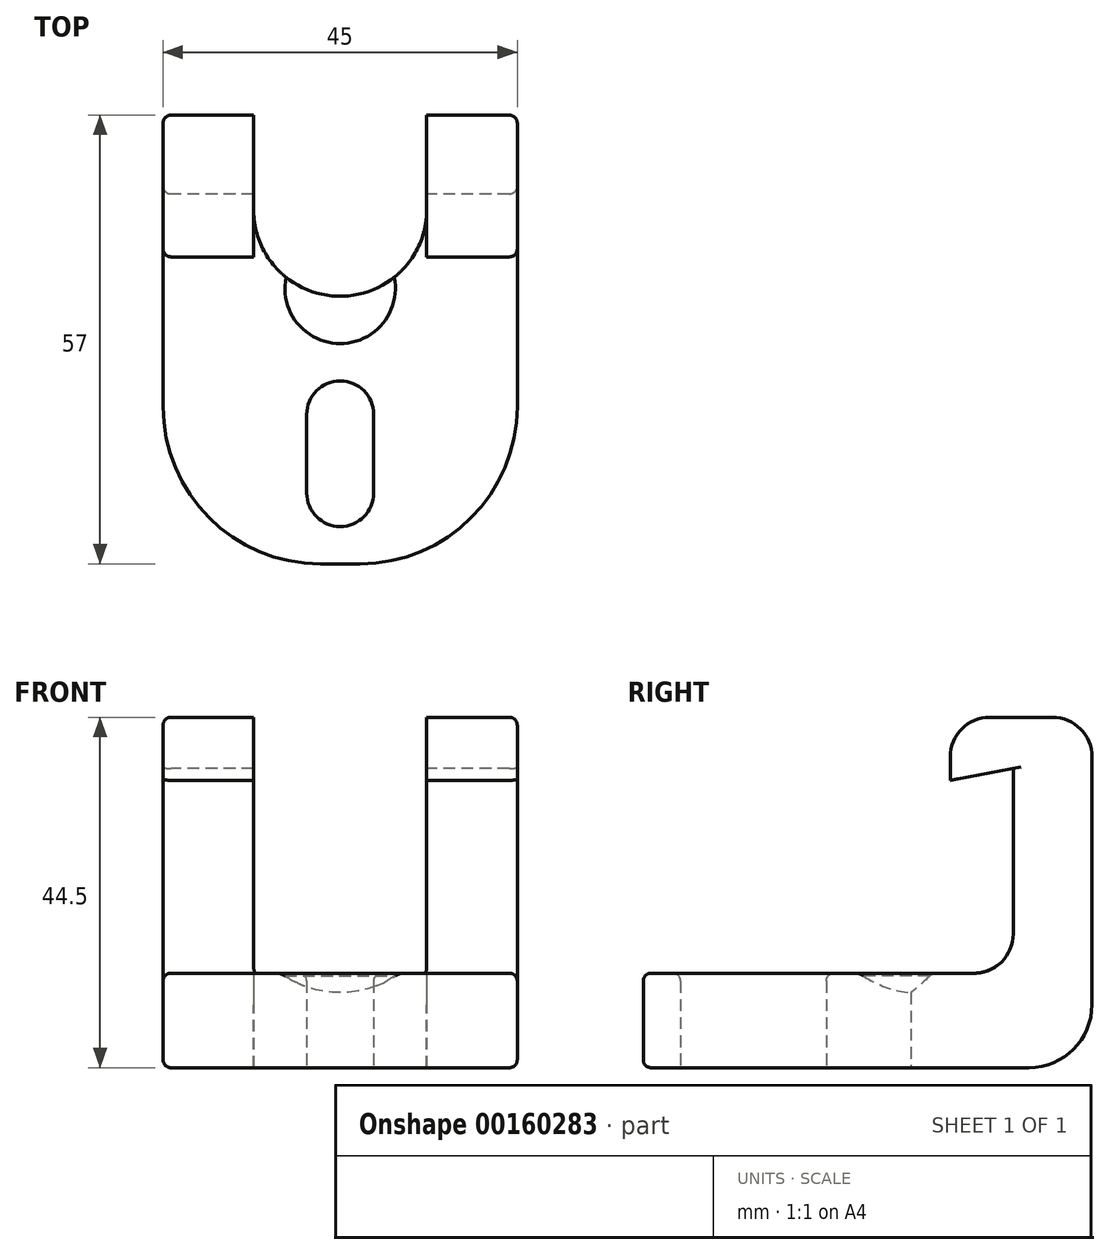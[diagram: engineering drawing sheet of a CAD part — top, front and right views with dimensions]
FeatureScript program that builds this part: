
annotation { "Feature Type Name" : "Feature", "Feature Type Description" : "" }
export const myFeature = defineFeature(function(context is Context, id is Id, definition is map)
    precondition{}
    {
        {
            var Q0;
            Q0=qCreatedBy(makeId("Right.planeOp"),FACE);
            var sketch = newSketch(context, id + "F0", { "sketchPlane" : qUnion([Q0])});
            skLineSegment(sketch, "E0", {"start": v(0, 0) * mm, "end": v(57, 0) * mm});
            skLineSegment(sketch, "E1", {"start": v(57, 0) * mm, "end": v(57, 44.5) * mm});
            skLineSegment(sketch, "E2", {"start": v(57, 44.5) * mm, "end": v(39, 44.5) * mm});
            skLineSegment(sketch, "E3", {"start": v(39, 44.5) * mm, "end": v(39, 36.5) * mm});
            skLineSegment(sketch, "E4", {"start": v(39, 36.5) * mm, "end": v(47, 38) * mm});
            skLineSegment(sketch, "E5", {"start": v(47, 38) * mm, "end": v(47, 12) * mm});
            skLineSegment(sketch, "E6", {"start": v(47, 12) * mm, "end": v(0, 12) * mm});
            skLineSegment(sketch, "E7", {"start": v(0, 12) * mm, "end": v(0, 0) * mm});
            skSolve(sketch);
        }
        {
            var Q0;
            Q0 = qSketchRegion(id + "F0", true);
            extrude(context, id + "F1", {"entities" : qUnion([Q0]), "depth" : 45 * mm});
        }
        {
            var Q0;
            Q0=makeQuery(id+"F1.opExtrude","SWEPT_FACE",FACE,{"disambiguationData":[OSD([sQuery(id+"F0.wireOp",EDGE,"E0")])]});
            var sketch = newSketch(context, id + "F2", { "sketchPlane" : qUnion([Q0])});
            skLineSegment(sketch, "E8.bottom", {"start": v(11.5, -57) * mm, "end": v(33.5, -57) * mm});
            skLineSegment(sketch, "E8.top", {"start": v(11.5, -45) * mm, "end": v(33.5, -45) * mm});
            skLineSegment(sketch, "E8.left", {"start": v(11.5, -57) * mm, "end": v(11.5, -45) * mm});
            skLineSegment(sketch, "E8.right", {"start": v(33.5, -57) * mm, "end": v(33.5, -45) * mm});
            skArc(sketch, "E9", {"start": v(33.5, -45) * mm, "mid": v(22.5, -34) * mm, "end": v(11.5, -45) * mm});
            skSolve(sketch);
        }
        {
            var Q0;
            Q0 = qSketchRegion(id + "F2", true);
            var Q1;
            Q1=makeQuery(id+"F1.opExtrude","SWEPT_FACE",FACE,{"disambiguationData":[OSD([sQuery(id+"F0.wireOp",EDGE,"E4")])]});
            extrude(context, id + "F3", {"entities" : qUnion([Q0]), "operationType" : NewBodyOperationType.REMOVE, "endBound" : BoundingType.UP_TO_SURFACE, "oppositeDirection" : true, "endBoundEntityFace" : qUnion([Q1]), "depth" : 25 * mm});
        }
        {
            var Q0;
            Q0=makeQuery(id+"F1.opExtrude","SWEPT_FACE",FACE,{"disambiguationData":[OSD([sQuery(id+"F0.wireOp",EDGE,"E1")])]});
            var sketch = newSketch(context, id + "F4", { "sketchPlane" : qUnion([Q0])});
            skLineSegment(sketch, "E10.bottom", {"start": v(-33.5, 31) * mm, "end": v(-11.5, 31) * mm});
            skLineSegment(sketch, "E10.top", {"start": v(-33.5, 44.5) * mm, "end": v(-11.5, 44.5) * mm});
            skLineSegment(sketch, "E10.left", {"start": v(-33.5, 31) * mm, "end": v(-33.5, 44.5) * mm});
            skLineSegment(sketch, "E10.right", {"start": v(-11.5, 31) * mm, "end": v(-11.5, 44.5) * mm});
            skSolve(sketch);
        }
        {
            var Q0;
            Q0 = qSketchRegion(id + "F4", true);
            extrude(context, id + "F5", {"entities" : qUnion([Q0]), "operationType" : NewBodyOperationType.REMOVE, "oppositeDirection" : true, "depth" : 25 * mm});
        }
        {
            var Q0;
            Q0=makeQuery(id+"F1.opExtrude","SWEPT_FACE",FACE,{"disambiguationData":[OSD([sQuery(id+"F0.wireOp",EDGE,"E0")])]});
            var sketch = newSketch(context, id + "F6", { "sketchPlane" : qUnion([Q0])});
            skCircle(sketch, "E11", {"center": v(22.5, -9) * mm, "radius": 4.25 * mm});
            skPoint(sketch, "E11.centerSnap0", {"position": v(22.5, 0) * mm});
            skLineSegment(sketch, "E12.bottom", {"start": v(18.25, -9) * mm, "end": v(26.75, -9) * mm});
            skLineSegment(sketch, "E12.top", {"start": v(18.25, -19) * mm, "end": v(26.75, -19) * mm});
            skLineSegment(sketch, "E12.left", {"start": v(18.25, -9) * mm, "end": v(18.25, -19) * mm});
            skLineSegment(sketch, "E12.right", {"start": v(26.75, -9) * mm, "end": v(26.75, -19) * mm});
            skCircle(sketch, "E13", {"center": v(22.5, -19) * mm, "radius": 4.25 * mm});
            skSolve(sketch);
        }
        {
            var Q0;
            {var subQ0=sQuery(id+"F6.wireOp",EDGE,"E12.bottom");Q0=makeQuery(id+"F6.imprint","IMPRINT",FACE,{"disambiguationData":[TD([[makeQuery(id+"F6.imprint","IMPRINT",EDGE,{"derivedFrom":subQ0}),1.0]])]});}
            var Q1;
            {var subQ0=sQuery(id+"F6.wireOp",EDGE,"E12.bottom");Q1=makeQuery(id+"F6.imprint","IMPRINT",FACE,{"disambiguationData":[TD([[makeQuery(id+"F6.imprint","IMPRINT",EDGE,{"derivedFrom":subQ0}),-1.0]])]});}
            var Q2;
            {var subQ0=sQuery(id+"F6.wireOp",EDGE,"E13");var subQ1=sQuery(id+"F6.wireOp",EDGE,"E11");var subQ2=makeQuery(id+"F6.imprint","INTERSECT",VERTEX,{"disambiguationData":[OD(0.0)],"derivedFrom":[subQ1,subQ0]});Q2=makeQuery(id+"F6.imprint","IMPRINT",FACE,{"disambiguationData":[TD([[makeQuery(id+"F6.imprint","IMPRINT",EDGE,{"disambiguationData":[TD([[subQ2,-1.0]])],"derivedFrom":subQ1}),1.0]])]});}
            var Q3;
            {var subQ0=sQuery(id+"F6.wireOp",EDGE,"E12.left");Q3=makeQuery(id+"F6.imprint","IMPRINT",FACE,{"disambiguationData":[TD([[makeQuery(id+"F6.imprint","IMPRINT",EDGE,{"derivedFrom":subQ0}),1.0]])]});}
            var Q4;
            {var subQ4=sQuery(id+"F6.wireOp",EDGE,"E12.top");Q4=makeQuery(id+"F6.imprint","IMPRINT",FACE,{"disambiguationData":[TD([[makeQuery(id+"F6.imprint","IMPRINT",EDGE,{"derivedFrom":subQ4}),1.0]])]});}
            var Q5;
            {var subQ0=sQuery(id+"F6.wireOp",EDGE,"E12.right");Q5=makeQuery(id+"F6.imprint","IMPRINT",FACE,{"disambiguationData":[TD([[makeQuery(id+"F6.imprint","IMPRINT",EDGE,{"derivedFrom":subQ0}),-1.0]])]});}
            var Q6;
            {var subQ0=sQuery(id+"F6.wireOp",EDGE,"E12.top");Q6=makeQuery(id+"F6.imprint","IMPRINT",FACE,{"disambiguationData":[TD([[makeQuery(id+"F6.imprint","IMPRINT",EDGE,{"derivedFrom":subQ0}),-1.0]])]});}
            extrude(context, id + "F7", {"entities" : qUnion([Q0, Q1, Q2, Q3, Q4, Q5, Q6]), "operationType" : NewBodyOperationType.REMOVE, "oppositeDirection" : true, "depth" : 25 * mm});
        }
        {
            var Q0;
            Q0=makeQuery(id+"F3.boolean.opBoolean","INTERSECT",EDGE,{"derivedFrom":[makeQuery(id+"F1.opExtrude","SWEPT_FACE",FACE,{"disambiguationData":[OSD([sQuery(id+"F0.wireOp",EDGE,"E6")])]}),makeQuery(id+"F3.opExtrude","SWEPT_FACE",FACE,{"disambiguationData":[OSD([sQuery(id+"F2.wireOp",EDGE,"E9")])]})]});
            cPoint(context, id + "F8", {"entities" : qUnion([Q0]), "parameter" : 0.5});
        }
        {
            var Q0;
            Q0=qCreatedBy(makeId("Right.planeOp"),FACE);
            var Q1;
            Q1 = qCreatedBy(id + "F8" ,VERTEX);
            cPlane(context, id + "F9", {"entities" : qUnion([Q0, Q1]), "cplaneType" : CPlaneType.PLANE_POINT, "offset" : 25 * mm, "width" : 150 * mm, "height" : 150 * mm});
        }
        {
            var Q0;
            Q0=qCreatedBy(id+"F9.planeOp",FACE);
            var sketch = newSketch(context, id + "F10", { "sketchPlane" : qUnion([Q0])});
            skCircle(sketch, "E14", {"center": v(35, 22) * mm, "radius": 12.5 * mm});
            skLineSegment(sketch, "E15", {"start": v(22.5, 22) * mm, "end": v(47.5, 22) * mm});
            skSolve(sketch);
        }
        {
            var Q0;
            {var subQ0=sQuery(id+"F10.wireOp",EDGE,"E15");Q0=makeQuery(id+"F10.imprint","IMPRINT",FACE,{"disambiguationData":[TD([[makeQuery(id+"F10.imprint","IMPRINT",EDGE,{"derivedFrom":subQ0}),-1.0]])]});}
            var Q1;
            Q1=sQuery(id+"F10.wireOp",EDGE,"E15");
            revolve(context, id + "F11", {"operationType" : NewBodyOperationType.REMOVE, "entities" : qUnion([Q0]), "axis" : qUnion([Q1]), "revolveType" : RevolveType.FULL, "oppositeDirection" : true});
        }
        {
            var Q0;
            Q0=makeQuery(id+"F1.opExtrude","CAP_EDGE",EDGE,{"disambiguationData":[OSD([sQuery(id+"F0.wireOp",EDGE,"E7")])],"isStart":false});
            var Q1;
            Q1=makeQuery(id+"F1.opExtrude","CAP_EDGE",EDGE,{"disambiguationData":[OSD([sQuery(id+"F0.wireOp",EDGE,"E7")])],"isStart":true});
            fillet(context, id + "F12", {"entities" : qUnion([Q0, Q1]), "radius" : 20 * mm, "tangentPropagation" : true, "allowEdgeOverflow" : false});
        }
        {
            var Q0;
            Q0=makeQuery(id+"F11.boolean.opBoolean","INTERSECT",EDGE,{"derivedFrom":[makeQuery(id+"F1.opExtrude","SWEPT_FACE",FACE,{"disambiguationData":[OSD([sQuery(id+"F0.wireOp",EDGE,"E6")])]}),makeQuery(id+"F11.opRevolve","SWEPT_FACE",FACE,{"disambiguationData":[OSD([sQuery(id+"F10.wireOp",EDGE,"E14")])]})]});
            fillet(context, id + "F13", {"entities" : qUnion([Q0]), "radius" : 2 * mm, "tangentPropagation" : true, "allowEdgeOverflow" : false});
        }
        {
            var Q0;
            {var subQ0=sQuery(id+"F0.wireOp",EDGE,"E6");var subQ1=sQuery(id+"F0.wireOp",EDGE,"E5");Q0=makeQuery(id+"F3.boolean.opBoolean","SPLIT",EDGE,{"disambiguationData":[TD([makeQuery(id+"F3.opExtrude","SWEPT_FACE",FACE,{"disambiguationData":[OSD([sQuery(id+"F2.wireOp",EDGE,"E8.left")])]})])],"derivedFrom":makeQuery(id+"F1.opExtrude","SWEPT_EDGE",EDGE,{"disambiguationData":[OSD([subQ1,subQ0])]})});}
            var Q1;
            {var subQ0=sQuery(id+"F0.wireOp",EDGE,"E6");var subQ1=sQuery(id+"F0.wireOp",EDGE,"E5");Q1=makeQuery(id+"F3.boolean.opBoolean","SPLIT",EDGE,{"disambiguationData":[TD([makeQuery(id+"F3.opExtrude","SWEPT_FACE",FACE,{"disambiguationData":[OSD([sQuery(id+"F2.wireOp",EDGE,"E8.right")])]})])],"derivedFrom":makeQuery(id+"F1.opExtrude","SWEPT_EDGE",EDGE,{"disambiguationData":[OSD([subQ1,subQ0])]})});}
            var Q2;
            {var subQ0=sQuery(id+"F0.wireOp",EDGE,"E2");var subQ1=sQuery(id+"F0.wireOp",EDGE,"E1");Q2=makeQuery(id+"F5.boolean.opBoolean","SPLIT",EDGE,{"disambiguationData":[TD([makeQuery(id+"F3.boolean.opBoolean","COPY",FACE,{"derivedFrom":makeQuery(id+"F3.opExtrude","SWEPT_FACE",FACE,{"disambiguationData":[OSD([sQuery(id+"F2.wireOp",EDGE,"E8.left")])]})})])],"derivedFrom":makeQuery(id+"F1.opExtrude","SWEPT_EDGE",EDGE,{"disambiguationData":[OSD([subQ1,subQ0])]})});}
            var Q3;
            {var subQ0=sQuery(id+"F0.wireOp",EDGE,"E2");var subQ1=sQuery(id+"F0.wireOp",EDGE,"E1");Q3=makeQuery(id+"F5.boolean.opBoolean","SPLIT",EDGE,{"disambiguationData":[TD([makeQuery(id+"F3.boolean.opBoolean","COPY",FACE,{"derivedFrom":makeQuery(id+"F3.opExtrude","SWEPT_FACE",FACE,{"disambiguationData":[OSD([sQuery(id+"F2.wireOp",EDGE,"E8.right")])]})})])],"derivedFrom":makeQuery(id+"F1.opExtrude","SWEPT_EDGE",EDGE,{"disambiguationData":[OSD([subQ1,subQ0])]})});}
            var Q4;
            {var subQ0=sQuery(id+"F0.wireOp",EDGE,"E3");var subQ1=sQuery(id+"F0.wireOp",EDGE,"E2");Q4=makeQuery(id+"F5.boolean.opBoolean","SPLIT",EDGE,{"disambiguationData":[TD([makeQuery(id+"F3.boolean.opBoolean","COPY",FACE,{"derivedFrom":makeQuery(id+"F3.opExtrude","SWEPT_FACE",FACE,{"disambiguationData":[OSD([sQuery(id+"F2.wireOp",EDGE,"E8.left")])]})})])],"derivedFrom":makeQuery(id+"F1.opExtrude","SWEPT_EDGE",EDGE,{"disambiguationData":[OSD([subQ1,subQ0])]})});}
            var Q5;
            {var subQ0=sQuery(id+"F0.wireOp",EDGE,"E3");var subQ1=sQuery(id+"F0.wireOp",EDGE,"E2");Q5=makeQuery(id+"F5.boolean.opBoolean","SPLIT",EDGE,{"disambiguationData":[TD([makeQuery(id+"F3.boolean.opBoolean","COPY",FACE,{"derivedFrom":makeQuery(id+"F3.opExtrude","SWEPT_FACE",FACE,{"disambiguationData":[OSD([sQuery(id+"F2.wireOp",EDGE,"E8.right")])]})})])],"derivedFrom":makeQuery(id+"F1.opExtrude","SWEPT_EDGE",EDGE,{"disambiguationData":[OSD([subQ1,subQ0])]})});}
            fillet(context, id + "F14", {"entities" : qUnion([Q0, Q1, Q2, Q3, Q4, Q5]), "radius" : 5 * mm, "tangentPropagation" : true, "allowEdgeOverflow" : false});
        }
        {
            var Q0;
            {var subQ0=sQuery(id+"F0.wireOp",EDGE,"E0");var subQ1=sQuery(id+"F0.wireOp",EDGE,"E1");Q0=makeQuery(id+"F3.boolean.opBoolean","SPLIT",EDGE,{"disambiguationData":[TD([makeQuery(id+"F3.opExtrude","SWEPT_FACE",FACE,{"disambiguationData":[OSD([sQuery(id+"F2.wireOp",EDGE,"E8.right")])]})])],"derivedFrom":makeQuery(id+"F1.opExtrude","SWEPT_EDGE",EDGE,{"disambiguationData":[OSD([subQ0,subQ1])]})});}
            var Q1;
            {var subQ0=sQuery(id+"F0.wireOp",EDGE,"E0");var subQ1=sQuery(id+"F0.wireOp",EDGE,"E1");Q1=makeQuery(id+"F3.boolean.opBoolean","SPLIT",EDGE,{"disambiguationData":[TD([makeQuery(id+"F3.opExtrude","SWEPT_FACE",FACE,{"disambiguationData":[OSD([sQuery(id+"F2.wireOp",EDGE,"E8.left")])]})])],"derivedFrom":makeQuery(id+"F1.opExtrude","SWEPT_EDGE",EDGE,{"disambiguationData":[OSD([subQ0,subQ1])]})});}
            fillet(context, id + "F15", {"entities" : qUnion([Q0, Q1]), "radius" : 8 * mm, "tangentPropagation" : true, "allowEdgeOverflow" : false});
        }
        {
            var Q0;
            Q0=makeQuery(id+"F1.opExtrude","CAP_EDGE",EDGE,{"disambiguationData":[OSD([sQuery(id+"F0.wireOp",EDGE,"E6")])],"isStart":false});
            var Q1;
            Q1=makeQuery(id+"F1.opExtrude","CAP_EDGE",EDGE,{"disambiguationData":[OSD([sQuery(id+"F0.wireOp",EDGE,"E0")])],"isStart":false});
            var Q2;
            Q2=makeQuery(id+"F3.boolean.opBoolean","COPY",EDGE,{"derivedFrom":makeQuery(id+"F3.opExtrude","CAP_EDGE",EDGE,{"disambiguationData":[OSD([sQuery(id+"F2.wireOp",EDGE,"E9")])],"isStart":true})});
            var Q3;
            Q3=makeQuery(id+"F3.boolean.opBoolean","INTERSECT",EDGE,{"derivedFrom":[makeQuery(id+"F1.opExtrude","SWEPT_FACE",FACE,{"disambiguationData":[OSD([sQuery(id+"F0.wireOp",EDGE,"E5")])]}),makeQuery(id+"F3.opExtrude","SWEPT_FACE",FACE,{"disambiguationData":[OSD([sQuery(id+"F2.wireOp",EDGE,"E8.right")])]})]});
            var Q4;
            Q4=makeQuery(id+"F7.boolean.opBoolean","COPY",EDGE,{"derivedFrom":makeQuery(id+"F7.opExtrude","CAP_EDGE",EDGE,{"disambiguationData":[OSD([sQuery(id+"F6.wireOp",EDGE,"E11")])],"isStart":true})});
            var Q5;
            Q5=makeQuery(id+"F7.boolean.opBoolean","INTERSECT",EDGE,{"derivedFrom":[makeQuery(id+"F1.opExtrude","SWEPT_FACE",FACE,{"disambiguationData":[OSD([sQuery(id+"F0.wireOp",EDGE,"E6")])]}),makeQuery(id+"F7.opExtrude","SWEPT_FACE",FACE,{"disambiguationData":[OSD([sQuery(id+"F6.wireOp",EDGE,"E11")])]})]});
            fillet(context, id + "F16", {"entities" : qUnion([Q0, Q1, Q2, Q3, Q4, Q5]), "radius" : 1 * mm, "tangentPropagation" : true, "allowEdgeOverflow" : false});
        }
    });
